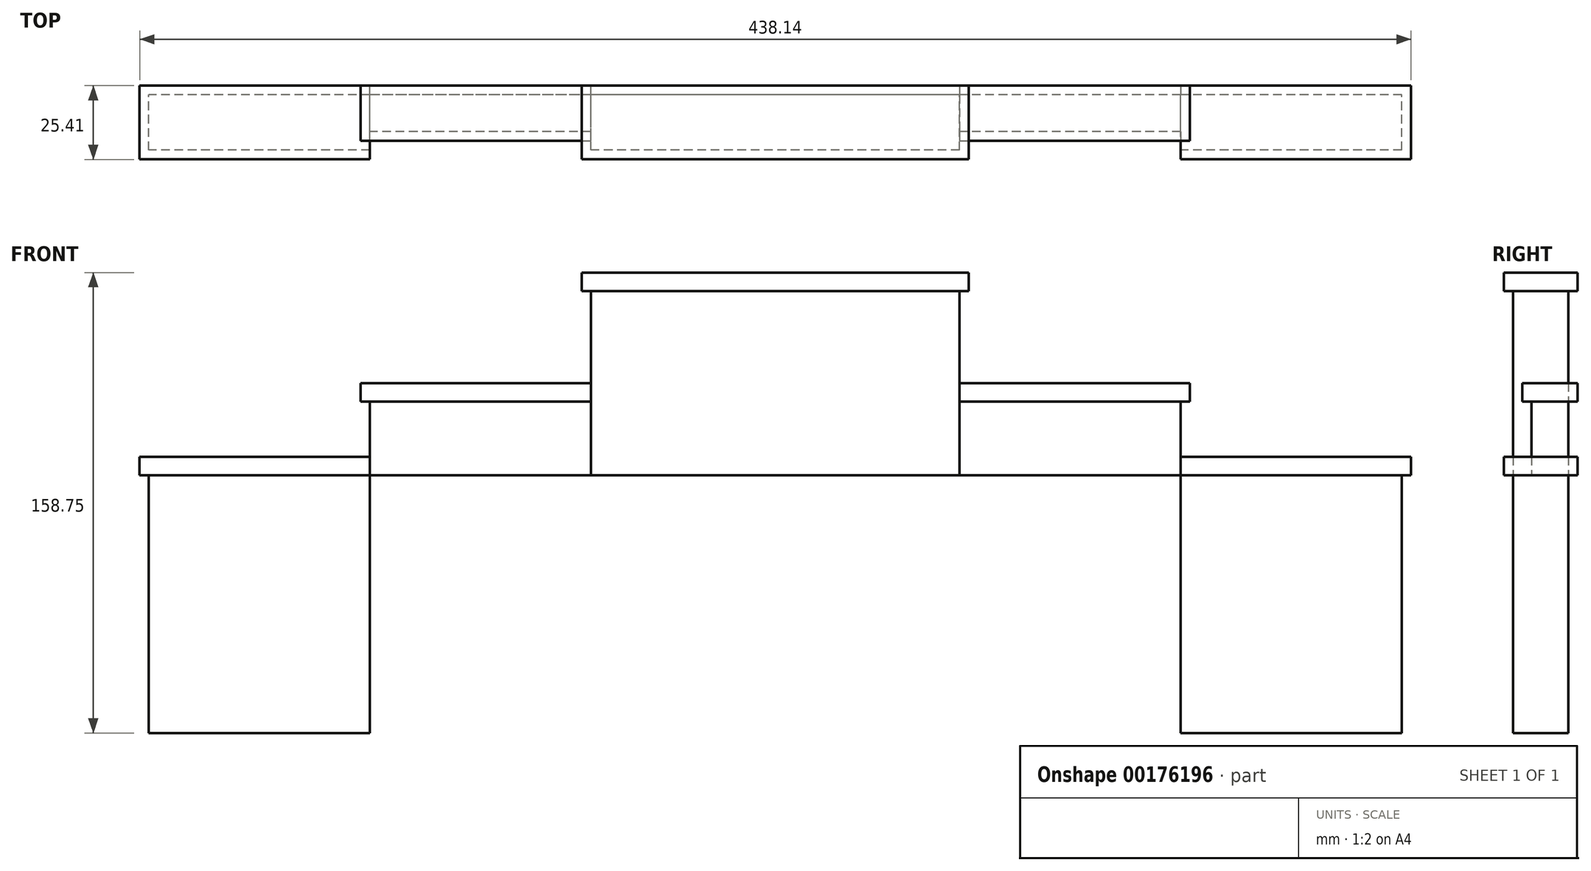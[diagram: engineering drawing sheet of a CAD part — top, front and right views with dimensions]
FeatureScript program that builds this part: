
annotation { "Feature Type Name" : "Feature", "Feature Type Description" : "" }
export const myFeature = defineFeature(function(context is Context, id is Id, definition is map)
    precondition{}
    {
        {
            var Q0;
            Q0=qCreatedBy(makeId("Front.planeOp"),FACE);
            var sketch = newSketch(context, id + "F0", { "sketchPlane" : qUnion([Q0])});
            skLineSegment(sketch, "E0.bottom", {"start": v(473.08, 0) * mm, "end": v(-473.08, 0) * mm, "construction": true});
            skLineSegment(sketch, "E0.top", {"start": v(473.08, 66.68) * mm, "end": v(-473.08, 66.68) * mm, "construction": true});
            skLineSegment(sketch, "E0.left", {"start": v(473.08, 66.68) * mm, "end": v(473.08, 0) * mm, "construction": true});
            skLineSegment(sketch, "E0.right", {"start": v(-473.08, 66.67) * mm, "end": v(-473.08, 0) * mm, "construction": true});
            skPoint(sketch, "E0.middle", {"position": v(0, 0) * mm});
            skLineSegment(sketch, "E1.bottom", {"start": v(63.5, 152.4) * mm, "end": v(-63.5, 152.4) * mm});
            skLineSegment(sketch, "E1.top", {"start": v(63.5, 0) * mm, "end": v(-63.5, 0) * mm});
            skLineSegment(sketch, "E1.left", {"start": v(63.5, 152.4) * mm, "end": v(63.5, 0) * mm});
            skLineSegment(sketch, "E1.right", {"start": v(-63.5, 152.4) * mm, "end": v(-63.5, 0) * mm});
            skPoint(sketch, "E1.middle", {"position": v(0, 76.2) * mm});
            skLineSegment(sketch, "E2.bottom", {"start": v(139.7, 114.3) * mm, "end": v(-139.7, 114.3) * mm});
            skLineSegment(sketch, "E2.top", {"start": v(139.7, 0) * mm, "end": v(-139.7, 0) * mm});
            skLineSegment(sketch, "E2.left", {"start": v(139.7, 114.3) * mm, "end": v(139.7, 0) * mm});
            skLineSegment(sketch, "E2.right", {"start": v(-139.7, 114.3) * mm, "end": v(-139.7, 0) * mm});
            skPoint(sketch, "E2.middle", {"position": v(0, 57.15) * mm});
            skLineSegment(sketch, "E3.bottom", {"start": v(215.9, 88.9) * mm, "end": v(-215.9, 88.9) * mm});
            skLineSegment(sketch, "E3.top", {"start": v(215.9, 0) * mm, "end": v(-215.9, 0) * mm});
            skLineSegment(sketch, "E3.left", {"start": v(215.9, 88.9) * mm, "end": v(215.9, 0) * mm});
            skLineSegment(sketch, "E3.right", {"start": v(-215.9, 88.9) * mm, "end": v(-215.9, 0) * mm});
            skPoint(sketch, "E3.middle", {"position": v(0, 44.45) * mm});
            skSolve(sketch);
        }
        {
            var Q0;
            {var subQ5=sQuery(id+"F0.wireOp",EDGE,"E3.right");Q0=makeQuery(id+"F0.imprint","IMPRINT",FACE,{"disambiguationData":[TD([[makeQuery(id+"F0.imprint","IMPRINT",EDGE,{"derivedFrom":subQ5}),1.0]])]});}
            var Q1;
            {var subQ5=sQuery(id+"F0.wireOp",EDGE,"E3.left");Q1=makeQuery(id+"F0.imprint","IMPRINT",FACE,{"disambiguationData":[TD([[makeQuery(id+"F0.imprint","IMPRINT",EDGE,{"derivedFrom":subQ5}),-1.0]])]});}
            extrude(context, id + "F1", {"entities" : qUnion([Q0, Q1]), "depth" : 19.05 * mm});
        }
        {
            var Q0;
            {var subQ0=sQuery(id+"F0.wireOp",EDGE,"E3.top");var subQ1=sQuery(id+"F0.wireOp",EDGE,"E1.right");var subQ2=makeQuery(id+"F0.imprint","INTERSECT",VERTEX,{"derivedFrom":[subQ1,subQ0]});Q0=makeQuery(id+"F0.imprint","IMPRINT",FACE,{"disambiguationData":[TD([[makeQuery(id+"F0.imprint","IMPRINT",EDGE,{"disambiguationData":[TD([[subQ2,1.0]])],"derivedFrom":subQ1}),-1.0]])]});}
            var Q1;
            {var subQ0=sQuery(id+"F0.wireOp",EDGE,"E2.bottom");var subQ1=sQuery(id+"F0.wireOp",EDGE,"E1.right");var subQ2=makeQuery(id+"F0.imprint","INTERSECT",VERTEX,{"derivedFrom":[subQ1,subQ0]});Q1=makeQuery(id+"F0.imprint","IMPRINT",FACE,{"disambiguationData":[TD([[makeQuery(id+"F0.imprint","IMPRINT",EDGE,{"disambiguationData":[TD([[subQ2,-1.0]])],"derivedFrom":subQ1}),-1.0]])]});}
            var Q2;
            {var subQ0=sQuery(id+"F0.wireOp",EDGE,"E2.bottom");var subQ1=sQuery(id+"F0.wireOp",EDGE,"E1.left");var subQ2=makeQuery(id+"F0.imprint","INTERSECT",VERTEX,{"derivedFrom":[subQ1,subQ0]});Q2=makeQuery(id+"F0.imprint","IMPRINT",FACE,{"disambiguationData":[TD([[makeQuery(id+"F0.imprint","IMPRINT",EDGE,{"disambiguationData":[TD([[subQ2,-1.0]])],"derivedFrom":subQ1}),1.0]])]});}
            var Q3;
            {var subQ0=sQuery(id+"F0.wireOp",EDGE,"E3.top");var subQ1=sQuery(id+"F0.wireOp",EDGE,"E1.left");var subQ2=makeQuery(id+"F0.imprint","INTERSECT",VERTEX,{"derivedFrom":[subQ1,subQ0]});Q3=makeQuery(id+"F0.imprint","IMPRINT",FACE,{"disambiguationData":[TD([[makeQuery(id+"F0.imprint","IMPRINT",EDGE,{"disambiguationData":[TD([[subQ2,1.0]])],"derivedFrom":subQ1}),1.0]])]});}
            extrude(context, id + "F2", {"entities" : qUnion([Q0, Q1, Q2, Q3]), "operationType" : NewBodyOperationType.ADD, "depth" : 12.7 * mm});
        }
        {
            var Q0;
            {var subQ0=sQuery(id+"F0.wireOp",EDGE,"E1.bottom");Q0=makeQuery(id+"F0.imprint","IMPRINT",FACE,{"disambiguationData":[TD([[makeQuery(id+"F0.imprint","IMPRINT",EDGE,{"derivedFrom":subQ0}),1.0]])]});}
            var Q1;
            {var subQ0=sQuery(id+"F0.wireOp",EDGE,"E2.bottom");var subQ1=sQuery(id+"F0.wireOp",EDGE,"E1.left");var subQ2=makeQuery(id+"F0.imprint","INTERSECT",VERTEX,{"derivedFrom":[subQ1,subQ0]});Q1=makeQuery(id+"F0.imprint","IMPRINT",FACE,{"disambiguationData":[TD([[makeQuery(id+"F0.imprint","IMPRINT",EDGE,{"disambiguationData":[TD([[subQ2,-1.0]])],"derivedFrom":subQ1}),-1.0]])]});}
            var Q2;
            {var subQ0=sQuery(id+"F0.wireOp",EDGE,"E3.top");var subQ1=sQuery(id+"F0.wireOp",EDGE,"E1.left");var subQ2=makeQuery(id+"F0.imprint","INTERSECT",VERTEX,{"derivedFrom":[subQ1,subQ0]});Q2=makeQuery(id+"F0.imprint","IMPRINT",FACE,{"disambiguationData":[TD([[makeQuery(id+"F0.imprint","IMPRINT",EDGE,{"disambiguationData":[TD([[subQ2,1.0]])],"derivedFrom":subQ1}),-1.0]])]});}
            extrude(context, id + "F3", {"entities" : qUnion([Q0, Q1, Q2]), "operationType" : NewBodyOperationType.ADD, "depth" : 19.05 * mm});
        }
        {
            var Q0;
            {var subQ0=sQuery(id+"F0.wireOp",EDGE,"E3.bottom");Q0=makeQuery(id+"F1.opExtrude","SWEPT_FACE",FACE,{"disambiguationData":[OSD([subQ0]),TDD([makeQuery(id+"F0.imprint","IMPRINT",EDGE,{"disambiguationData":[TD([[makeQuery(id+"F0.imprint","INTERSECT",VERTEX,{"derivedFrom":[subQ0,sQuery(id+"F0.wireOp",EDGE,"E3.right")]}),1.0]])],"derivedFrom":subQ0})])]});}
            var sketch = newSketch(context, id + "F4", { "sketchPlane" : qUnion([Q0])});
            skLineSegment(sketch, "E4.bottom", {"start": v(-219.08, 3.17) * mm, "end": v(-139.7, 3.18) * mm});
            skLineSegment(sketch, "E4.top", {"start": v(-219.08, -22.23) * mm, "end": v(-139.7, -22.22) * mm});
            skLineSegment(sketch, "E4.left", {"start": v(-219.08, 3.17) * mm, "end": v(-219.08, -22.23) * mm});
            skLineSegment(sketch, "E4.right", {"start": v(-139.7, 3.18) * mm, "end": v(-139.7, -22.22) * mm});
            skLineSegment(sketch, "E5.bottom", {"start": v(139.7, 3.18) * mm, "end": v(219.08, 3.18) * mm});
            skLineSegment(sketch, "E5.top", {"start": v(139.7, -22.22) * mm, "end": v(219.08, -22.22) * mm});
            skLineSegment(sketch, "E5.left", {"start": v(139.7, 3.18) * mm, "end": v(139.7, -22.22) * mm});
            skLineSegment(sketch, "E5.right", {"start": v(219.08, 3.18) * mm, "end": v(219.08, -22.22) * mm});
            skSolve(sketch);
        }
        {
            var Q0;
            {var subQ0=sQuery(id+"F0.wireOp",EDGE,"E3.right");var subQ1=sQuery(id+"F0.wireOp",EDGE,"E3.bottom");Q0=makeQuery(id+"F4.imprint","IMPRINT",FACE,{"disambiguationData":[TD([[makeQuery(id+"F4.imprint","IMPRINT",EDGE,{"derivedFrom":makeQuery(id+"F1.opExtrude","SWEPT_EDGE",EDGE,{"disambiguationData":[OSD([subQ1,subQ0])]})}),-1.0]])]});}
            var Q1;
            {var subQ5=sQuery(id+"F4.wireOp",EDGE,"E4.bottom");Q1=makeQuery(id+"F4.imprint","IMPRINT",FACE,{"disambiguationData":[TD([[makeQuery(id+"F4.imprint","IMPRINT",EDGE,{"derivedFrom":subQ5}),-1.0]])]});}
            var Q2;
            Q2=makeQuery(id+"F4.imprint","IMPRINT",FACE,{"disambiguationData":[TD([[makeQuery(id+"F4.imprint","IMPRINT",EDGE,{"derivedFrom":sQuery(id+"F4.wireOp",EDGE,"E5.bottom")}),-1.0]])]});
            extrude(context, id + "F5", {"entities" : qUnion([Q0, Q1, Q2]), "operationType" : NewBodyOperationType.ADD, "depth" : 6.35 * mm});
        }
        {
            var Q0;
            {var subQ0=sQuery(id+"F0.wireOp",EDGE,"E2.bottom");Q0=makeQuery(id+"F2.opExtrude","SWEPT_FACE",FACE,{"disambiguationData":[OSD([subQ0]),TDD([makeQuery(id+"F0.imprint","IMPRINT",EDGE,{"disambiguationData":[TD([[makeQuery(id+"F0.imprint","INTERSECT",VERTEX,{"derivedFrom":[subQ0,sQuery(id+"F0.wireOp",EDGE,"E2.right")]}),1.0]])],"derivedFrom":subQ0})])]});}
            var sketch = newSketch(context, id + "F6", { "sketchPlane" : qUnion([Q0])});
            skLineSegment(sketch, "E6.bottom", {"start": v(-142.88, 3.17) * mm, "end": v(-63.5, 3.18) * mm});
            skLineSegment(sketch, "E6.top", {"start": v(-142.88, -15.88) * mm, "end": v(-63.5, -15.87) * mm});
            skLineSegment(sketch, "E6.left", {"start": v(-142.88, 3.17) * mm, "end": v(-142.88, -15.88) * mm});
            skLineSegment(sketch, "E6.right", {"start": v(-63.5, 3.18) * mm, "end": v(-63.5, -15.87) * mm});
            skLineSegment(sketch, "E7.bottom", {"start": v(63.5, 3.18) * mm, "end": v(142.88, 3.18) * mm});
            skLineSegment(sketch, "E7.top", {"start": v(63.5, -15.87) * mm, "end": v(142.88, -15.87) * mm});
            skLineSegment(sketch, "E7.left", {"start": v(63.5, 3.18) * mm, "end": v(63.5, -15.87) * mm});
            skLineSegment(sketch, "E7.right", {"start": v(142.88, 3.18) * mm, "end": v(142.88, -15.87) * mm});
            skSolve(sketch);
        }
        {
            var Q0;
            {var subQ1=sQuery(id+"F0.wireOp",EDGE,"E2.right");var subQ2=sQuery(id+"F0.wireOp",EDGE,"E2.bottom");Q0=makeQuery(id+"F6.imprint","IMPRINT",FACE,{"disambiguationData":[TD([[makeQuery(id+"F6.imprint","IMPRINT",EDGE,{"derivedFrom":makeQuery(id+"F2.opExtrude","SWEPT_EDGE",EDGE,{"disambiguationData":[OSD([subQ2,subQ1])]})}),-1.0]])]});}
            var Q1;
            {var subQ5=sQuery(id+"F6.wireOp",EDGE,"E6.bottom");Q1=makeQuery(id+"F6.imprint","IMPRINT",FACE,{"disambiguationData":[TD([[makeQuery(id+"F6.imprint","IMPRINT",EDGE,{"derivedFrom":subQ5}),-1.0]])]});}
            var Q2;
            Q2=makeQuery(id+"F6.imprint","IMPRINT",FACE,{"disambiguationData":[TD([[makeQuery(id+"F6.imprint","IMPRINT",EDGE,{"derivedFrom":sQuery(id+"F6.wireOp",EDGE,"E7.bottom")}),-1.0]])]});
            extrude(context, id + "F7", {"entities" : qUnion([Q0, Q1, Q2]), "operationType" : NewBodyOperationType.ADD, "depth" : 6.35 * mm});
        }
        {
            var Q0;
            Q0=makeQuery(id+"F3.opExtrude","SWEPT_FACE",FACE,{"disambiguationData":[OSD([sQuery(id+"F0.wireOp",EDGE,"E1.bottom")])]});
            var sketch = newSketch(context, id + "F8", { "sketchPlane" : qUnion([Q0])});
            skLineSegment(sketch, "E8.bottom", {"start": v(-66.67, 3.17) * mm, "end": v(66.68, 3.18) * mm});
            skLineSegment(sketch, "E8.top", {"start": v(-66.67, -22.23) * mm, "end": v(66.68, -22.22) * mm});
            skLineSegment(sketch, "E8.left", {"start": v(-66.67, 3.17) * mm, "end": v(-66.67, -22.23) * mm});
            skLineSegment(sketch, "E8.right", {"start": v(66.68, 3.18) * mm, "end": v(66.68, -22.22) * mm});
            skSolve(sketch);
        }
        {
            var Q0;
            Q0=makeQuery(id+"F8.imprint","IMPRINT",FACE,{"disambiguationData":[TD([[makeQuery(id+"F8.imprint","IMPRINT",EDGE,{"derivedFrom":sQuery(id+"F8.wireOp",EDGE,"E8.bottom")}),-1.0]])]});
            var Q1;
            {var subQ0=sQuery(id+"F0.wireOp",EDGE,"E1.bottom");Q1=makeQuery(id+"F8.imprint","IMPRINT",FACE,{"disambiguationData":[TD([[makeQuery(id+"F8.imprint","IMPRINT",EDGE,{"derivedFrom":makeQuery(id+"F3.opExtrude","CAP_EDGE",EDGE,{"disambiguationData":[OSD([subQ0])],"isStart":true})}),1.0]])]});}
            extrude(context, id + "F9", {"entities" : qUnion([Q0, Q1]), "operationType" : NewBodyOperationType.ADD, "depth" : 6.35 * mm});
        }
    });
